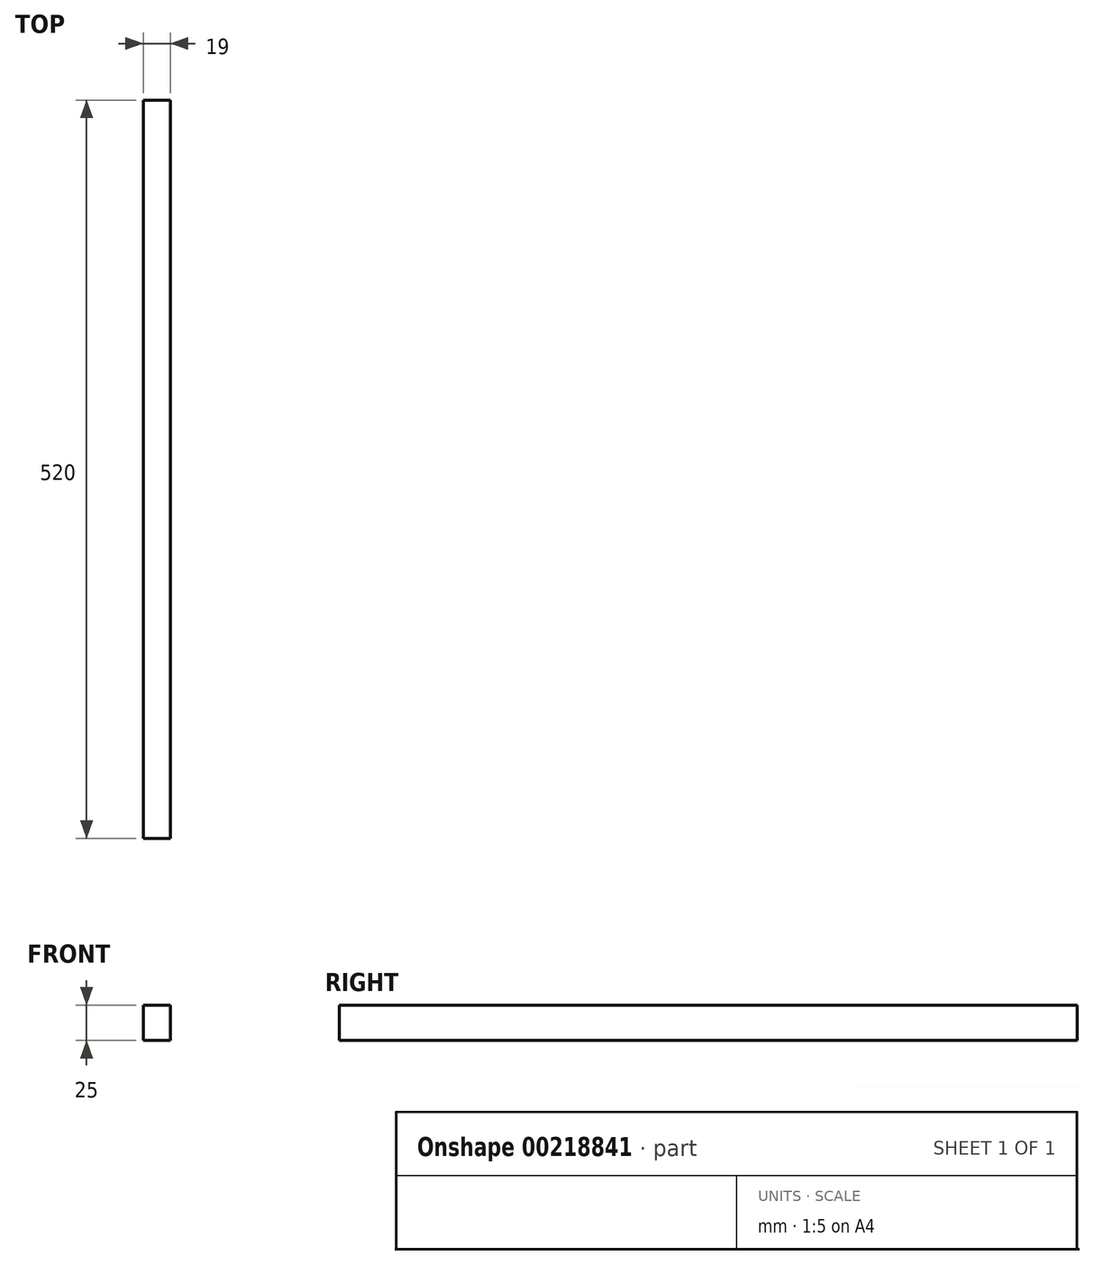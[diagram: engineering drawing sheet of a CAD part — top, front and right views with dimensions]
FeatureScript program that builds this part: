
annotation { "Feature Type Name" : "Feature", "Feature Type Description" : "" }
export const myFeature = defineFeature(function(context is Context, id is Id, definition is map)
    precondition{}
    {
        {
            var Q0;
            Q0=qCreatedBy(makeId("Front.planeOp"),FACE);
            var sketch = newSketch(context, id + "F0", { "sketchPlane" : qUnion([Q0])});
            skLineSegment(sketch, "E0.bottom", {"start": v(-45.39, 26.12) * mm, "end": v(-26.39, 26.12) * mm});
            skLineSegment(sketch, "E0.top", {"start": v(-45.39, 1.12) * mm, "end": v(-26.39, 1.12) * mm});
            skLineSegment(sketch, "E0.left", {"start": v(-45.39, 26.12) * mm, "end": v(-45.39, 1.12) * mm});
            skLineSegment(sketch, "E0.right", {"start": v(-26.39, 26.12) * mm, "end": v(-26.39, 1.12) * mm});
            skSolve(sketch);
        }
        {
            var Q0;
            Q0=makeQuery(id+"F0.imprint","IMPRINT",FACE,{"disambiguationData":[TD([[makeQuery(id+"F0.imprint","IMPRINT",EDGE,{"derivedFrom":sQuery(id+"F0.wireOp",EDGE,"E0.bottom")}),-1.0]])]});
            extrude(context, id + "F1", {"entities" : qUnion([Q0]), "oppositeDirection" : true, "depth" : 520 * mm});
        }
    });
